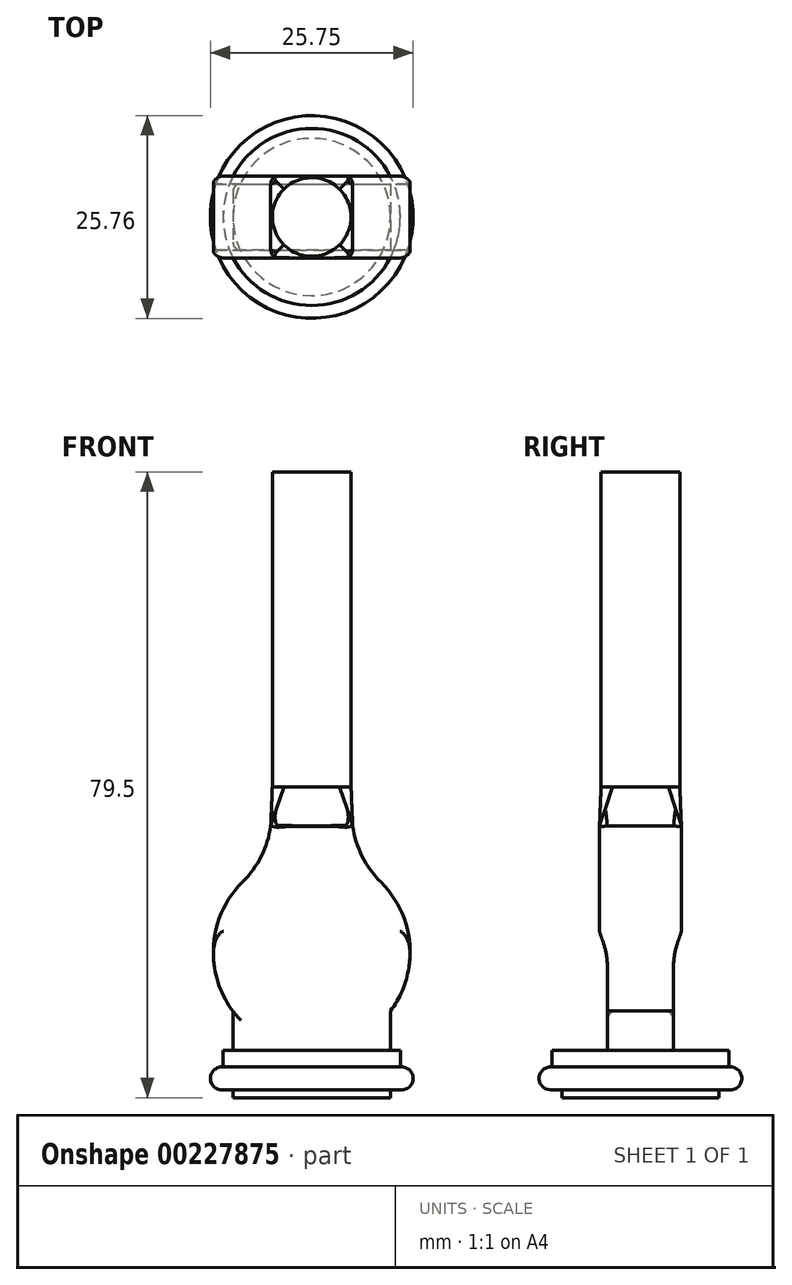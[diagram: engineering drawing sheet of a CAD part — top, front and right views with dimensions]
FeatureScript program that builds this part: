
annotation { "Feature Type Name" : "Feature", "Feature Type Description" : "" }
export const myFeature = defineFeature(function(context is Context, id is Id, definition is map)
    precondition{}
    {
        {
            var Q0;
            Q0=qCreatedBy(makeId("Right.planeOp"),FACE);
            var sketch = newSketch(context, id + "F0", { "sketchPlane" : qUnion([Q0])});
            skLineSegment(sketch, "E0", {"start": v(0, 0) * mm, "end": v(11.42, 0) * mm});
            skArc(sketch, "E1", {"start": v(11.43, 2.9) * mm, "mid": v(12.88, 1.45) * mm, "end": v(11.43, 0) * mm});
            skLineSegment(sketch, "E2", {"start": v(0, 0) * mm, "end": v(0, 10.64) * mm});
            skLineSegment(sketch, "E3", {"start": v(11.43, 0) * mm, "end": v(11.43, 2.9) * mm});
            skLineSegment(sketch, "E4", {"start": v(11.43, 2.9) * mm, "end": v(0, 2.9) * mm});
            skLineSegment(sketch, "E5", {"start": v(0, 0) * mm, "end": v(0, 2.9) * mm});
            skPoint(sketch, "E6.start.orphan", {"position": v(0, 2.9) * mm});
            skSolve(sketch);
        }
        {
            var Q0;
            Q0=qSketchRegion(id+"F0",true);
            var Q1;
            Q1=sQuery(id+"F0.wireOp",EDGE,"E5");
            revolve(context, id + "F1", {"entities" : qUnion([Q0]), "axis" : qUnion([Q1]), "revolveType" : RevolveType.FULL});
        }
        {
            var Q0;
            Q0=makeQuery(id+"F1.opRevolve","SWEPT_FACE",FACE,{"disambiguationData":[OSD([sQuery(id+"F0.wireOp",EDGE,"E0")])]});
            var sketch = newSketch(context, id + "F2", { "sketchPlane" : qUnion([Q0])});
            skCircle(sketch, "E7", {"center": v(0, 0) * mm, "radius": 10 * mm});
            skSolve(sketch);
        }
        {
            var Q0;
            Q0=makeQuery(id+"F2.imprint","IMPRINT",FACE,{"disambiguationData":[TD([[makeQuery(id+"F2.imprint","IMPRINT",EDGE,{"derivedFrom":sQuery(id+"F2.wireOp",EDGE,"E7")}),1.0]])]});
            extrude(context, id + "F3", {"entities" : qUnion([Q0]), "operationType" : NewBodyOperationType.ADD, "depth" : 1 * mm});
        }
        {
            var Q0;
            Q0=makeQuery(id+"F1.opRevolve","SWEPT_FACE",FACE,{"disambiguationData":[OSD([sQuery(id+"F0.wireOp",EDGE,"E4")])]});
            var sketch = newSketch(context, id + "F4", { "sketchPlane" : qUnion([Q0])});
            skCircle(sketch, "E8", {"center": v(0, 0) * mm, "radius": 11.25 * mm});
            skSolve(sketch);
        }
        {
            var Q0;
            Q0=qSketchRegion(id+"F4",true);
            extrude(context, id + "F5", {"entities" : qUnion([Q0]), "operationType" : NewBodyOperationType.ADD, "depth" : 2.1 * mm});
        }
        {
            var Q0;
            Q0=makeQuery(id+"F5.opExtrude","CAP_FACE",FACE,{"disambiguationData":[OSD([sQuery(id+"F4.wireOp",EDGE,"E8")])],"isStart":false});
            var sketch = newSketch(context, id + "F6", { "sketchPlane" : qUnion([Q0])});
            skLineSegment(sketch, "E9.bottom", {"start": v(-10, 4.2) * mm, "end": v(10, 4.2) * mm});
            skLineSegment(sketch, "E9.top", {"start": v(-10, -4.2) * mm, "end": v(10, -4.2) * mm});
            skLineSegment(sketch, "E9.left", {"start": v(-10, 4.2) * mm, "end": v(-10, -4.2) * mm});
            skLineSegment(sketch, "E9.right", {"start": v(10, 4.2) * mm, "end": v(10, -4.2) * mm});
            skPoint(sketch, "E9.middle", {"position": v(0, 0) * mm});
            skSolve(sketch);
        }
        {
            var Q0;
            Q0=makeQuery(id+"F6.imprint","IMPRINT",FACE,{"disambiguationData":[TD([[makeQuery(id+"F6.imprint","IMPRINT",EDGE,{"derivedFrom":sQuery(id+"F6.wireOp",EDGE,"E9.bottom")}),-1.0]])]});
            extrude(context, id + "F7", {"entities" : qUnion([Q0]), "operationType" : NewBodyOperationType.ADD, "depth" : 5 * mm});
        }
        {
            var Q0;
            Q0=makeQuery(id+"F7.opExtrude","SWEPT_FACE",FACE,{"disambiguationData":[OSD([sQuery(id+"F6.wireOp",EDGE,"E9.top")])]});
            var sketch = newSketch(context, id + "F8", { "sketchPlane" : qUnion([Q0])});
            skLineSegment(sketch, "E10", {"start": v(0, 17.5) * mm, "end": v(0, 5) * mm, "construction": true});
            skLineSegment(sketch, "E11", {"start": v(0, 17.5) * mm, "end": v(12.5, 17.5) * mm});
            skLineSegment(sketch, "E12.MirrorCS", {"start": v(0, 17.5) * mm, "end": v(-12.5, 17.5) * mm});
            skArc(sketch, "E13", {"start": v(-12.5, 17.5) * mm, "mid": v(0, 5) * mm, "end": v(12.5, 17.5) * mm});
            skLineSegment(sketch, "E14", {"start": v(0, 17.5) * mm, "end": v(0, 33.5) * mm, "construction": true});
            skLineSegment(sketch, "E15", {"start": v(0, 33.5) * mm, "end": v(-5.2, 33.5) * mm});
            skLineSegment(sketch, "E16.MirrorCS", {"start": v(0, 33.5) * mm, "end": v(5.2, 33.5) * mm});
            skArc(sketch, "E17", {"start": v(-8.79, 26.39) * mm, "mid": v(0, 5) * mm, "end": v(8.79, 26.39) * mm});
            skArc(sketch, "E18", {"start": v(5.2, 33.5) * mm, "mid": v(6.41, 29.65) * mm, "end": v(8.79, 26.39) * mm});
            skArc(sketch, "E19.MirrorCS", {"start": v(-5.2, 33.5) * mm, "mid": v(-6.41, 29.65) * mm, "end": v(-8.79, 26.39) * mm});
            skSolve(sketch);
        }
        {
            var Q0;
            {var subQ1=sQuery(id+"F6.wireOp",EDGE,"E9.top");var subQ2=makeQuery(id+"F7.opExtrude","CAP_EDGE",EDGE,{"disambiguationData":[OSD([subQ1])],"isStart":false});Q0=makeQuery(id+"F8.imprint","IMPRINT",FACE,{"disambiguationData":[TD([[makeQuery(id+"F8.imprint","IMPRINT",EDGE,{"derivedFrom":subQ2}),1.0]])]});}
            var Q1;
            {var subQ1=sQuery(id+"F6.wireOp",EDGE,"E9.top");var subQ2=makeQuery(id+"F7.opExtrude","CAP_EDGE",EDGE,{"disambiguationData":[OSD([subQ1])],"isStart":false});Q1=makeQuery(id+"F8.imprint","IMPRINT",FACE,{"disambiguationData":[TD([[makeQuery(id+"F8.imprint","IMPRINT",EDGE,{"derivedFrom":subQ2}),-1.0]])]});}
            var Q2;
            Q2=makeQuery(id+"F7.opExtrude","SWEPT_FACE",FACE,{"disambiguationData":[OSD([sQuery(id+"F6.wireOp",EDGE,"E9.bottom")])]});
            extrude(context, id + "F9", {"entities" : qUnion([Q0, Q1]), "operationType" : NewBodyOperationType.ADD, "endBound" : BoundingType.UP_TO_SURFACE, "oppositeDirection" : true, "endBoundEntityFace" : qUnion([Q2]), "depth" : 11 * mm});
        }
        {
            var Q0;
            {var subQ0=sQuery(id+"F8.wireOp",EDGE,"E12.MirrorCS");Q0=makeQuery(id+"F8.imprint","IMPRINT",FACE,{"disambiguationData":[TD([[makeQuery(id+"F8.imprint","IMPRINT",EDGE,{"derivedFrom":subQ0}),-1.0]])]});}
            var Q1;
            {var subQ0=sQuery(id+"F8.wireOp",EDGE,"E11");Q1=makeQuery(id+"F8.imprint","IMPRINT",FACE,{"disambiguationData":[TD([[makeQuery(id+"F8.imprint","IMPRINT",EDGE,{"derivedFrom":subQ0}),1.0]])]});}
            extrude(context, id + "F10", {"entities" : qUnion([Q0, Q1]), "operationType" : NewBodyOperationType.ADD, "oppositeDirection" : true, "depth" : 9.4 * mm, "hasSecondDirection" : true, "secondDirectionOppositeDirection" : false, "secondDirectionDepth" : 1 * mm});
        }
        {
            var Q0;
            Q0=makeQuery(id+"F10.opExtrude","CAP_EDGE",EDGE,{"disambiguationData":[OSD([sQuery(id+"F8.wireOp",EDGE,"E11"),sQuery(id+"F8.wireOp",EDGE,"E12.MirrorCS")])],"isStart":true});
            var Q1;
            Q1=makeQuery(id+"F10.opExtrude","CAP_EDGE",EDGE,{"disambiguationData":[OSD([sQuery(id+"F8.wireOp",EDGE,"E11"),sQuery(id+"F8.wireOp",EDGE,"E12.MirrorCS")])],"isStart":false});
            fillet(context, id + "F11", {"entities" : qUnion([Q0, Q1]), "radius" : 4 * mm, "tangentPropagation" : true, "rho" : 0.1, "crossSection" : FilletCrossSection.CONIC, "allowEdgeOverflow" : false});
        }
        {
            var Q0;
            {var subQ0=sQuery(id+"F6.wireOp",EDGE,"E9.bottom");Q0=makeQuery(id+"F11.opFillet","BLEND_EDGE",EDGE,{"blendedFrom":[makeQuery(id+"F10.opExtrude","CAP_EDGE",EDGE,{"disambiguationData":[OSD([sQuery(id+"F8.wireOp",EDGE,"E11"),sQuery(id+"F8.wireOp",EDGE,"E12.MirrorCS")])],"isStart":false}),makeQuery(id+"F9.boolean.opBoolean","MERGE",FACE,{"derivedFrom":[makeQuery(id+"F7.opExtrude","SWEPT_FACE",FACE,{"disambiguationData":[OSD([subQ0])]}),makeQuery(id+"F9.opExtrude","CAP_FACE",FACE,{"disambiguationData":[OSD([subQ0])],"isStart":false})]})],"blendedInto":[makeQuery(id+"F9.boolean.opBoolean","MERGE",FACE,{"derivedFrom":[makeQuery(id+"F7.opExtrude","SWEPT_FACE",FACE,{"disambiguationData":[OSD([subQ0])]}),makeQuery(id+"F9.opExtrude","CAP_FACE",FACE,{"disambiguationData":[OSD([subQ0])],"isStart":false})]})]});}
            var Q1;
            {var subQ0=sQuery(id+"F8.wireOp",EDGE,"E12.MirrorCS");var subQ1=sQuery(id+"F8.wireOp",EDGE,"E11");Q1=makeQuery(id+"F11.opFillet","BLEND_EDGE",EDGE,{"blendedFrom":[makeQuery(id+"F10.opExtrude","CAP_EDGE",EDGE,{"disambiguationData":[OSD([subQ1,subQ0])],"isStart":true}),makeQuery(id+"F9.boolean.opBoolean","MERGE",FACE,{"derivedFrom":[makeQuery(id+"F7.opExtrude","SWEPT_FACE",FACE,{"disambiguationData":[OSD([sQuery(id+"F6.wireOp",EDGE,"E9.top")])]}),makeQuery(id+"F9.opExtrude","CAP_FACE",FACE,{"disambiguationData":[OSD([subQ1,subQ0,sQuery(id+"F8.wireOp",EDGE,"E17")])],"isStart":true})]})],"blendedInto":[makeQuery(id+"F9.boolean.opBoolean","MERGE",FACE,{"derivedFrom":[makeQuery(id+"F7.opExtrude","SWEPT_FACE",FACE,{"disambiguationData":[OSD([sQuery(id+"F6.wireOp",EDGE,"E9.top")])]}),makeQuery(id+"F9.opExtrude","CAP_FACE",FACE,{"disambiguationData":[OSD([subQ1,subQ0,sQuery(id+"F8.wireOp",EDGE,"E17")])],"isStart":true})]})]});}
            fillet(context, id + "F12", {"entities" : qUnion([Q0, Q1]), "radius" : 10 * mm, "tangentPropagation" : true, "allowEdgeOverflow" : false});
        }
        {
            var Q0;
            Q0=makeQuery(id+"F10.opExtrude","SWEPT_FACE",FACE,{"disambiguationData":[OSD([sQuery(id+"F8.wireOp",EDGE,"E15"),sQuery(id+"F8.wireOp",EDGE,"E16.MirrorCS")])]});
            var sketch = newSketch(context, id + "F13", { "sketchPlane" : qUnion([Q0])});
            skLineSegment(sketch, "E20.bottom", {"start": v(-5.2, -5.2) * mm, "end": v(5.2, -5.2) * mm});
            skLineSegment(sketch, "E20.top", {"start": v(-5.2, 5.2) * mm, "end": v(5.2, 5.2) * mm});
            skLineSegment(sketch, "E20.left", {"start": v(-5.2, -5.2) * mm, "end": v(-5.2, 5.2) * mm});
            skLineSegment(sketch, "E20.right", {"start": v(5.2, -5.2) * mm, "end": v(5.2, 5.2) * mm});
            skSolve(sketch);
        }
        {
            var Q0;
            Q0=makeQuery(id+"F10.opExtrude","SWEPT_FACE",FACE,{"disambiguationData":[OSD([sQuery(id+"F8.wireOp",EDGE,"E15"),sQuery(id+"F8.wireOp",EDGE,"E16.MirrorCS")])]});
            cPlane(context, id + "F14", {"entities" : qUnion([Q0]), "cplaneType" : CPlaneType.OFFSET, "offset" : 5 * mm, "width" : 150 * mm, "height" : 150 * mm});
        }
        {
            var Q0;
            Q0=qCreatedBy(id+"F14.planeOp",FACE);
            var sketch = newSketch(context, id + "F15", { "sketchPlane" : qUnion([Q0])});
            skCircle(sketch, "E21", {"center": v(0, 0) * mm, "radius": 5 * mm});
            skSolve(sketch);
        }
        {
            var Q1;
            Q1=qSketchRegion(id+"F15",true);
            var Q2;
            Q2=qSketchRegion(id+"F13",true);
            loft(context, id + "F16", {"operationType" : NewBodyOperationType.ADD, "sheetProfilesArray" : [{ "sheetProfileEntities" : qUnion([Q1]) }, { "sheetProfileEntities" : qUnion([Q2]) }]});
        }
        {
            var Q0;
            Q0=makeQuery(id+"F10.opExtrude","CAP_FACE",FACE,{"disambiguationData":[OSD([sQuery(id+"F8.wireOp",EDGE,"E11"),sQuery(id+"F8.wireOp",EDGE,"E12.MirrorCS"),sQuery(id+"F8.wireOp",EDGE,"E15"),sQuery(id+"F8.wireOp",EDGE,"E16.MirrorCS"),sQuery(id+"F8.wireOp",EDGE,"E17"),sQuery(id+"F8.wireOp",EDGE,"E18"),sQuery(id+"F8.wireOp",EDGE,"E19.MirrorCS")])],"isStart":false});
            var Q1;
            Q1=makeQuery(id+"F10.opExtrude","CAP_FACE",FACE,{"disambiguationData":[OSD([sQuery(id+"F8.wireOp",EDGE,"E11"),sQuery(id+"F8.wireOp",EDGE,"E12.MirrorCS"),sQuery(id+"F8.wireOp",EDGE,"E15"),sQuery(id+"F8.wireOp",EDGE,"E16.MirrorCS"),sQuery(id+"F8.wireOp",EDGE,"E17"),sQuery(id+"F8.wireOp",EDGE,"E18"),sQuery(id+"F8.wireOp",EDGE,"E19.MirrorCS")])],"isStart":true});
            var Q2;
            Q2=makeQuery(id+"F7.opExtrude","CAP_EDGE",EDGE,{"disambiguationData":[OSD([sQuery(id+"F6.wireOp",EDGE,"E9.right")])],"isStart":false});
            var Q3;
            Q3=makeQuery(id+"F7.opExtrude","SWEPT_EDGE",EDGE,{"disambiguationData":[OSD([sQuery(id+"FuZsFtzNlm9TGJ4_0.wireOp",EDGE,"divp8c7Z-MUNg-e6nj-06QF-rrWpHvL2V2d9"),sQuery(id+"F0.wireOp",EDGE,"E1"),sQuery(id+"F0.wireOp",EDGE,"E3"),sQuery(id+"F6.wireOp",EDGE,"E9.bottom"),sQuery(id+"F6.wireOp",EDGE,"E9.left")])]});
            var Q4;
            Q4=makeQuery(id+"F7.opExtrude","SWEPT_EDGE",EDGE,{"disambiguationData":[OSD([sQuery(id+"FuZsFtzNlm9TGJ4_0.wireOp",EDGE,"divp8c7Z-MUNg-e6nj-06QF-rrWpHvL2V2d9"),sQuery(id+"F0.wireOp",EDGE,"E1"),sQuery(id+"F0.wireOp",EDGE,"E3"),sQuery(id+"F6.wireOp",EDGE,"E9.top"),sQuery(id+"F6.wireOp",EDGE,"E9.left")])]});
            fillet(context, id + "F17", {"entities" : qUnion([Q0, Q1, Q2, Q3, Q4]), "radius" : 1 * mm, "tangentPropagation" : true, "allowEdgeOverflow" : false});
        }
        {
            var Q0;
            Q0=qSketchRegion(id+"F15",true);
            extrude(context, id + "F18", {"entities" : qUnion([Q0]), "operationType" : NewBodyOperationType.ADD, "depth" : 40 * mm});
        }
    });
